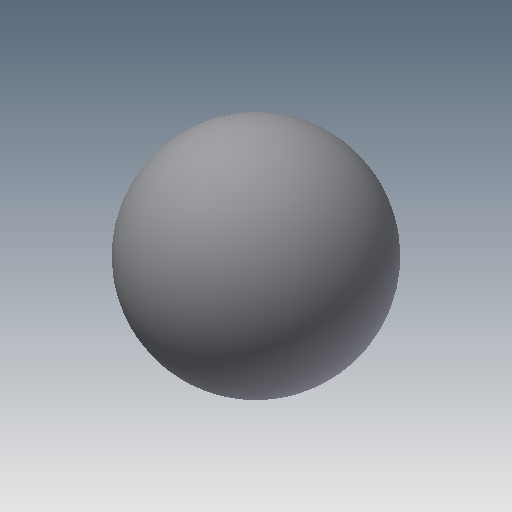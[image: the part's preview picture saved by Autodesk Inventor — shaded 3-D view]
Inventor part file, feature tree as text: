
AUTODESK INVENTOR PART (.ipt)
format: ipt  version: 2019.4 (Build 234330000, 330)  size: 142,848 bytes
history: native  units: mm
features: other x7, revolve x1, sketch x1
ambient origin geometry x8: Origin, YZ Plane, XZ Plane, XY Plane, X Axis, Y Axis, Z Axis, Center Point
bodies: Solid1 (feature_tree)
feature tree (9):
  revolve  "Revolution1"  [1 undecoded]
  other  "1_XY"
  other  "1_YZ"
  other  "1_ZX"
  other  "1_X"
  other  "1_Y"
  other  "1_Z"
  other  "1_Center"
  sketch  "Sketch_1"  dims[d0=360.0deg]
note: 1 required parameter value undecoded (feature->parameter linkage not recoverable at this tier; creation-order binding heuristic only, values carry confidence <= 0.55)
